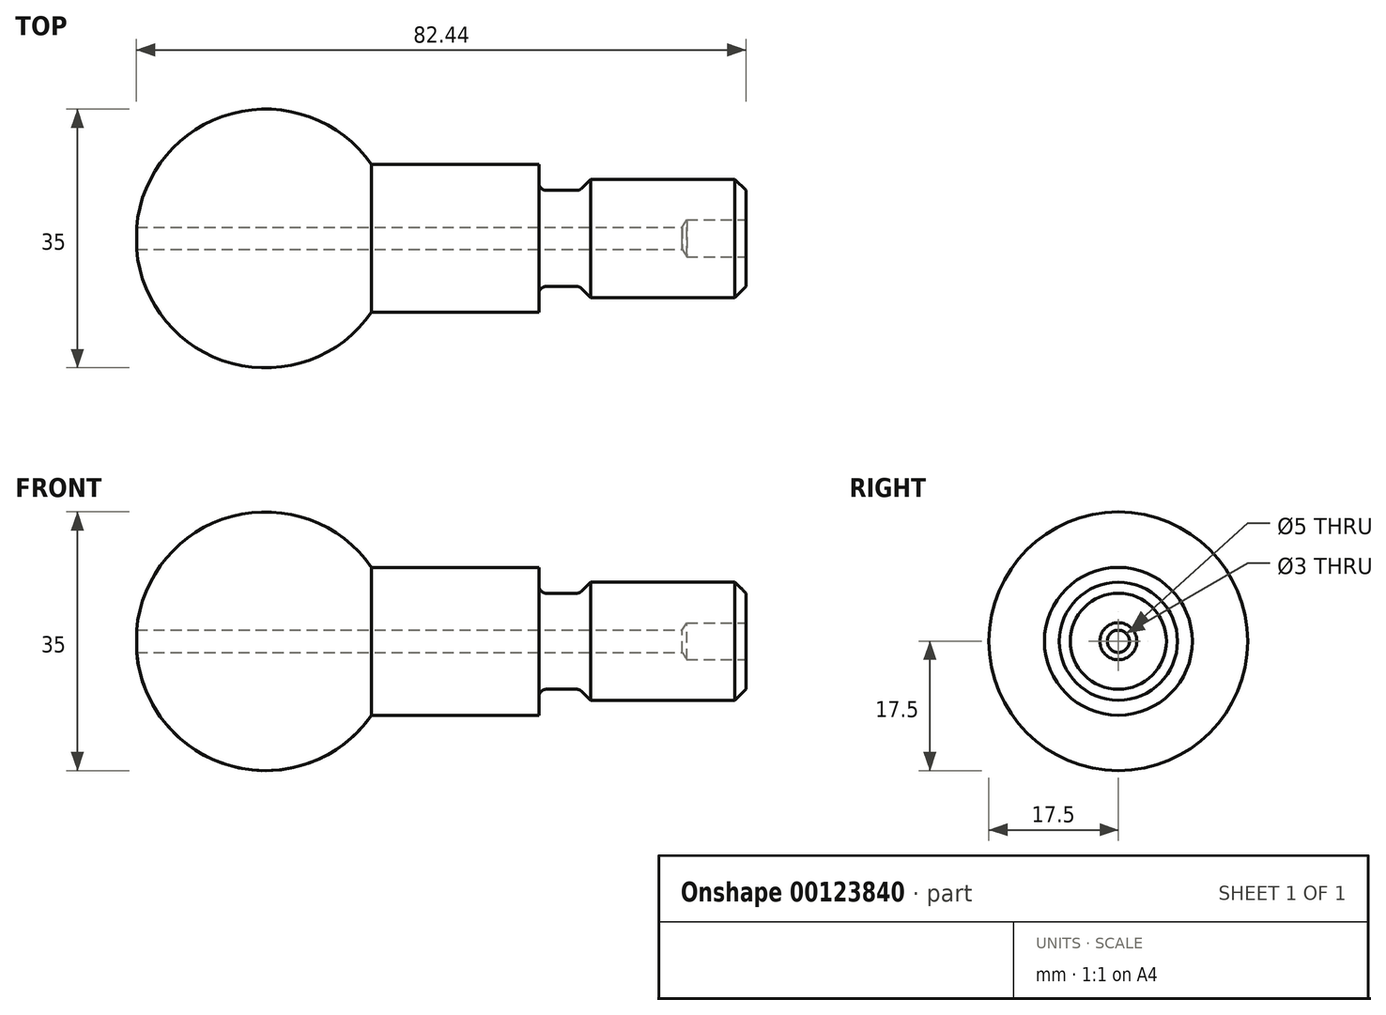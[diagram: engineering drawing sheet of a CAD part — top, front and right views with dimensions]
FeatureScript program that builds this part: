
annotation { "Feature Type Name" : "Feature", "Feature Type Description" : "" }
export const myFeature = defineFeature(function(context is Context, id is Id, definition is map)
    precondition{}
    {
        {
            var Q0;
            Q0=qCreatedBy(makeId("Top.planeOp"),FACE);
            var sketch = newSketch(context, id + "F0", { "sketchPlane" : qUnion([Q0])});
            skLineSegment(sketch, "E0", {"start": v(0, 0) * mm, "end": v(82.5, 0) * mm});
            skLineSegment(sketch, "E1", {"start": v(82.5, 0) * mm, "end": v(82.5, 8) * mm});
            skLineSegment(sketch, "E2", {"start": v(82.5, 8) * mm, "end": v(61.5, 8) * mm});
            skLineSegment(sketch, "E3", {"start": v(61.5, 8) * mm, "end": v(60, 6.5) * mm});
            skLineSegment(sketch, "E4", {"start": v(60, 6.5) * mm, "end": v(54.5, 6.5) * mm});
            skLineSegment(sketch, "E5", {"start": v(54.5, 6.5) * mm, "end": v(54.5, 10) * mm});
            skLineSegment(sketch, "E6", {"start": v(54.5, 10) * mm, "end": v(31.86, 10) * mm});
            skArc(sketch, "E7", {"start": v(31.86, 10) * mm, "mid": v(12.26, 16.7) * mm, "end": v(0, 0) * mm});
            skCircle(sketch, "E8", {"center": v(17.5, 0) * mm, "radius": 17.5 * mm, "construction": true});
            skSolve(sketch);
        }
        {
            var Q0;
            Q0 = qSketchRegion(id + "F0", true);
            var Q1;
            Q1=sQuery(id+"F0.wireOp",EDGE,"E0");
            revolve(context, id + "F1", {"entities" : qUnion([Q0]), "axis" : qUnion([Q1]), "revolveType" : RevolveType.FULL});
        }
        {
            var Q0;
            Q0=makeQuery(id+"F1.opRevolve","SWEPT_FACE",FACE,{"disambiguationData":[OSD([sQuery(id+"F0.wireOp",EDGE,"E1")])]});
            var sketch = newSketch(context, id + "F2", { "sketchPlane" : qUnion([Q0])});
            skCircle(sketch, "E9.0", {"center": v(0, 0) * mm, "radius": 8 * mm});
            skSolve(sketch);
        }
        {
            var Q0;
            Q0=sQuery(id+"F2.wireOp",VERTEX,"E9.0.center");
            var Q1;
            Q1=makeQuery(id+"F1.opRevolve","SWEPT_BODY",BODY,{"disambiguationData":[OSD([sQuery(id+"F0.wireOp",EDGE,"E0"),sQuery(id+"F0.wireOp",EDGE,"E1"),sQuery(id+"F0.wireOp",EDGE,"E2"),sQuery(id+"F0.wireOp",EDGE,"E3"),sQuery(id+"F0.wireOp",EDGE,"E4"),sQuery(id+"F0.wireOp",EDGE,"E5"),sQuery(id+"F0.wireOp",EDGE,"E6"),sQuery(id+"F0.wireOp",EDGE,"E7")])]});
            hole(context, id + "F3", {"style" : HoleStyle.SIMPLE, "endStyle" : HoleEndStyle.BLIND, "holeDiameter" : 5 * mm, "holeDepth" : 8 * mm, "startFromSketch" : true, "locations" : qUnion([Q0]), "scope" : qUnion([Q1]), "majorDiameter" : 5 * mm, "tappedDepth" : 12 * mm, "tapClearance" : 3});
        }
        {
            var Q0;
            Q0=sQuery(id+"F2.wireOp",VERTEX,"E9.0.center");
            var Q1;
            Q1=makeQuery(id+"F1.opRevolve","SWEPT_BODY",BODY,{"disambiguationData":[OSD([sQuery(id+"F0.wireOp",EDGE,"E0"),sQuery(id+"F0.wireOp",EDGE,"E1"),sQuery(id+"F0.wireOp",EDGE,"E2"),sQuery(id+"F0.wireOp",EDGE,"E3"),sQuery(id+"F0.wireOp",EDGE,"E4"),sQuery(id+"F0.wireOp",EDGE,"E5"),sQuery(id+"F0.wireOp",EDGE,"E6"),sQuery(id+"F0.wireOp",EDGE,"E7")])]});
            hole(context, id + "F4", {"style" : HoleStyle.SIMPLE, "endStyle" : HoleEndStyle.THROUGH, "holeDiameter" : 3 * mm, "startFromSketch" : true, "locations" : qUnion([Q0]), "scope" : qUnion([Q1]), "isTappedThrough" : true});
        }
        {
            var Q0;
            Q0=makeQuery(id+"F1.opRevolve","SWEPT_EDGE",EDGE,{"disambiguationData":[OSD([sQuery(id+"F0.wireOp",EDGE,"E4"),sQuery(id+"F0.wireOp",EDGE,"E5")])]});
            var Q1;
            Q1=makeQuery(id+"F1.opRevolve","SWEPT_EDGE",EDGE,{"disambiguationData":[OSD([sQuery(id+"F0.wireOp",EDGE,"E3"),sQuery(id+"F0.wireOp",EDGE,"E4")])]});
            fillet(context, id + "F5", {"entities" : qUnion([Q0, Q1]), "radius" : 1 * mm, "tangentPropagation" : true, "allowEdgeOverflow" : false});
        }
        {
            var Q0;
            Q0=makeQuery(id+"F1.opRevolve","SWEPT_EDGE",EDGE,{"disambiguationData":[OSD([sQuery(id+"F0.wireOp",EDGE,"E1"),sQuery(id+"F0.wireOp",EDGE,"E2")])]});
            chamfer(context, id + "F6", {"entities" : qUnion([Q0]), "width" : 1.5 * mm, "tangentPropagation" : true});
        }
    });
